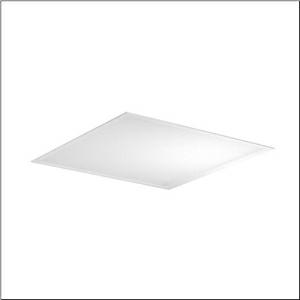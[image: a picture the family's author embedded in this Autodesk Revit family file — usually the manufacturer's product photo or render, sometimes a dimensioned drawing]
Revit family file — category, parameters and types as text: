
# Revit family: apollon_31_square_51mp12wd2342
name_source: partatom
category: Lighting Fixtures
units: mm (PartAtom-declared; Revit-internal decimal feet)

## family parameters
Cut with Voids When Loaded = No
Host = Face
Light Source = No
Part Type = Normal
Room Calculation Point = No
Round Connector Dimension = Use Diameter
Shared = No

## types (1)
- Apollon 31 square (1 x LED, 3600 lm, 27.5 W, 3000K)
    Apparent Load = 28 VA
    CIE Flux Codes = 61 87 97 100 100
    Color Rendering = 80
    Color Temperature = 3000K
    Default Elevation = 1800 mm
    Description = Apollon 31 square, office luminaire, primary optical cover: micro prismatic cover, of PMMA, CAT 2 (L<= 3000cd/m²), light emission: direct distribution, primary light characteristic: symmetric, installation type: lay-in mounting, recessed, LED, rated luminous flux: 3.600lm, luminous efficacy: 130lm/W, light colour: 830, colour temperature: 3000K, control gear: DALI 2, Multilumen, with terminal, 5-pole, mains connection: 220..240V, AC/DC, 0/50..60Hz, rated input power: 27.5W, suitable for self-contained emergency lighting element 58DB00B013A with integrated self-test function according to EN 60598-2-22, housing, of aluminium, coated, traffic white (RAL 9016), module: M600, length: 595mm, width: 595mm, height: 62mm, housing upper side, of sheet steel, coated, protection rating (complete): IP20, protection rating (lamp compartment, on room side): IP40, insulation class (complete): insulation class II (safety insulation), certification: CE, ENEC, impact resistance: IK03, permissible operating ambient temperature: -20..+40°C, standard: EN 60598-2-22, corresponds to IFS (International Featured Standards) requirements for safety and quality in the food industry, packaging unit: 1 piece
    Height = 0 mm  [stored 0 ft]
    Lamp = 1 x LED
    Lamp Light Flux = 3600 lm
    Lamp Power = 27.5 W
    Lamp count = 1
    Length = 595 mm
    Luminous efficacy = 131 lm/W
    Manufacturer = Siteco
    ModVariant = No
    Model = 51MP12WD2342
    Mounting Place = Ceiling
    Mounting Type = Recessed
    Number of Poles = 1
    OnlyDefault = Yes
    Power Factor = 1
    Product Name = Apollon 31 square
    Product group = office luminaire | ceiling recessed
    ProductGroupID = 400
    Protection Class = Protection class II
    Protection Degree = IP 20
    RLX_Detail_Level = 1
    RLX_Emergency_Light_Flux = 0 lm
    RLX_Emergency_Type = 0
    RLX_Emergency_Type_DB = No
    RlxData = <blob elided: 12861 chars, md5=8b6e7b3a>
    Socket = socket
    Standby Power = 0 W
    System Light Flux = 3600 lm
    System Power = 28 W
    Type Comments = Product without accessories
    Type Image = l_1291035.jpg
    URL = http://relux.com
    VarID = ---
    Voltage = 0 V
    Weight = 0.00 kg
    Width = 595 mm

note: [stored X ft] marks values corroborated as IEEE doubles in the binary element streams (Revit-internal decimal feet)

## geometry (parser evidence)
native form markers: Sweep x10
no freeform markers — native parametric forms only
